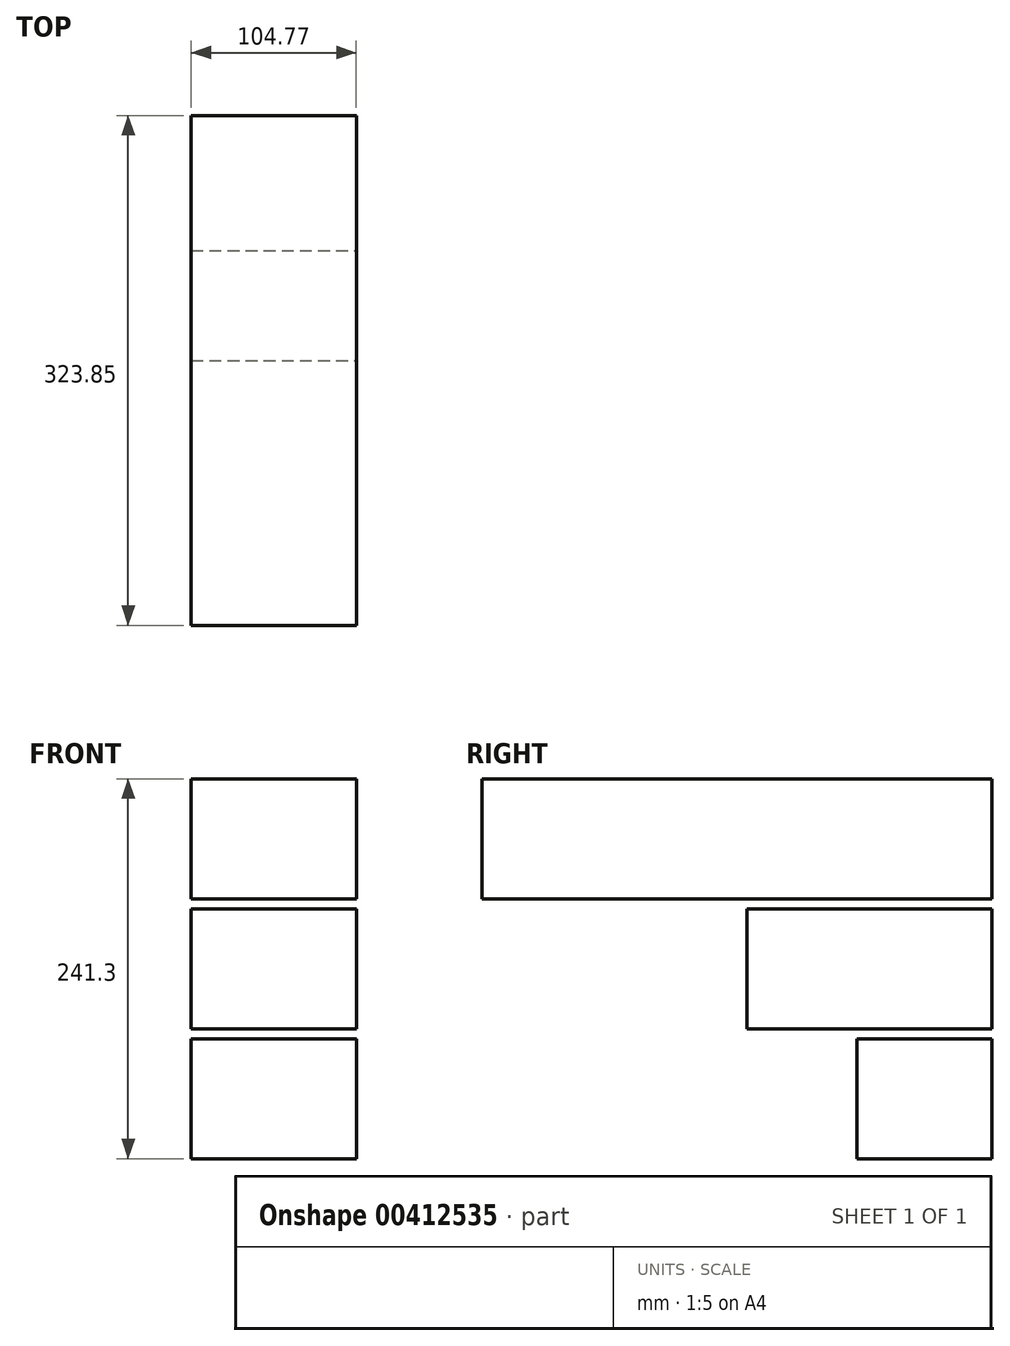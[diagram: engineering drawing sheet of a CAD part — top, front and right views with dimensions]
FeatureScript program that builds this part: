
annotation { "Feature Type Name" : "Feature", "Feature Type Description" : "" }
export const myFeature = defineFeature(function(context is Context, id is Id, definition is map)
    precondition{}
    {
        {
            var Q0;
            Q0=qCreatedBy(makeId("Front.planeOp"),FACE);
            var sketch = newSketch(context, id + "F0", { "sketchPlane" : qUnion([Q0])});
            skLineSegment(sketch, "E0.bottom", {"start": v(0, 0) * mm, "end": v(104.78, 0) * mm});
            skLineSegment(sketch, "E0.top", {"start": v(0, 76.2) * mm, "end": v(104.77, 76.2) * mm});
            skLineSegment(sketch, "E0.left", {"start": v(0, 0) * mm, "end": v(0, 76.2) * mm});
            skLineSegment(sketch, "E0.right", {"start": v(104.78, 0) * mm, "end": v(104.77, 76.2) * mm});
            skSolve(sketch);
        }
        {
            var Q0;
            Q0 = qSketchRegion(id + "F0", true);
            extrude(context, id + "F1", {"entities" : qUnion([Q0]), "depth" : 85.72 * mm});
        }
        {
            var Q0;
            Q0=qCreatedBy(makeId("Front.planeOp"),FACE);
            var sketch = newSketch(context, id + "F2", { "sketchPlane" : qUnion([Q0])});
            skLineSegment(sketch, "E1.bottom", {"start": v(0, 82.55) * mm, "end": v(104.78, 82.55) * mm});
            skLineSegment(sketch, "E1.top", {"start": v(0, 158.75) * mm, "end": v(104.78, 158.75) * mm});
            skLineSegment(sketch, "E1.left", {"start": v(0, 82.55) * mm, "end": v(0, 158.75) * mm});
            skLineSegment(sketch, "E1.right", {"start": v(104.78, 82.55) * mm, "end": v(104.77, 158.75) * mm});
            skSolve(sketch);
        }
        {
            var Q0;
            Q0 = qSketchRegion(id + "F2", true);
            extrude(context, id + "F3", {"entities" : qUnion([Q0]), "depth" : 155.57 * mm});
        }
        {
            var Q0;
            Q0=qCreatedBy(makeId("Front.planeOp"),FACE);
            var sketch = newSketch(context, id + "F4", { "sketchPlane" : qUnion([Q0])});
            skLineSegment(sketch, "E2.bottom", {"start": v(0, 165.1) * mm, "end": v(104.78, 165.1) * mm});
            skLineSegment(sketch, "E2.top", {"start": v(0, 241.3) * mm, "end": v(104.77, 241.3) * mm});
            skLineSegment(sketch, "E2.left", {"start": v(0, 165.1) * mm, "end": v(0, 241.3) * mm});
            skLineSegment(sketch, "E2.right", {"start": v(104.78, 165.1) * mm, "end": v(104.77, 241.3) * mm});
            skSolve(sketch);
        }
        {
            var Q0;
            Q0 = qSketchRegion(id + "F4", true);
            extrude(context, id + "F5", {"entities" : qUnion([Q0]), "depth" : 323.85 * mm});
        }
    });
